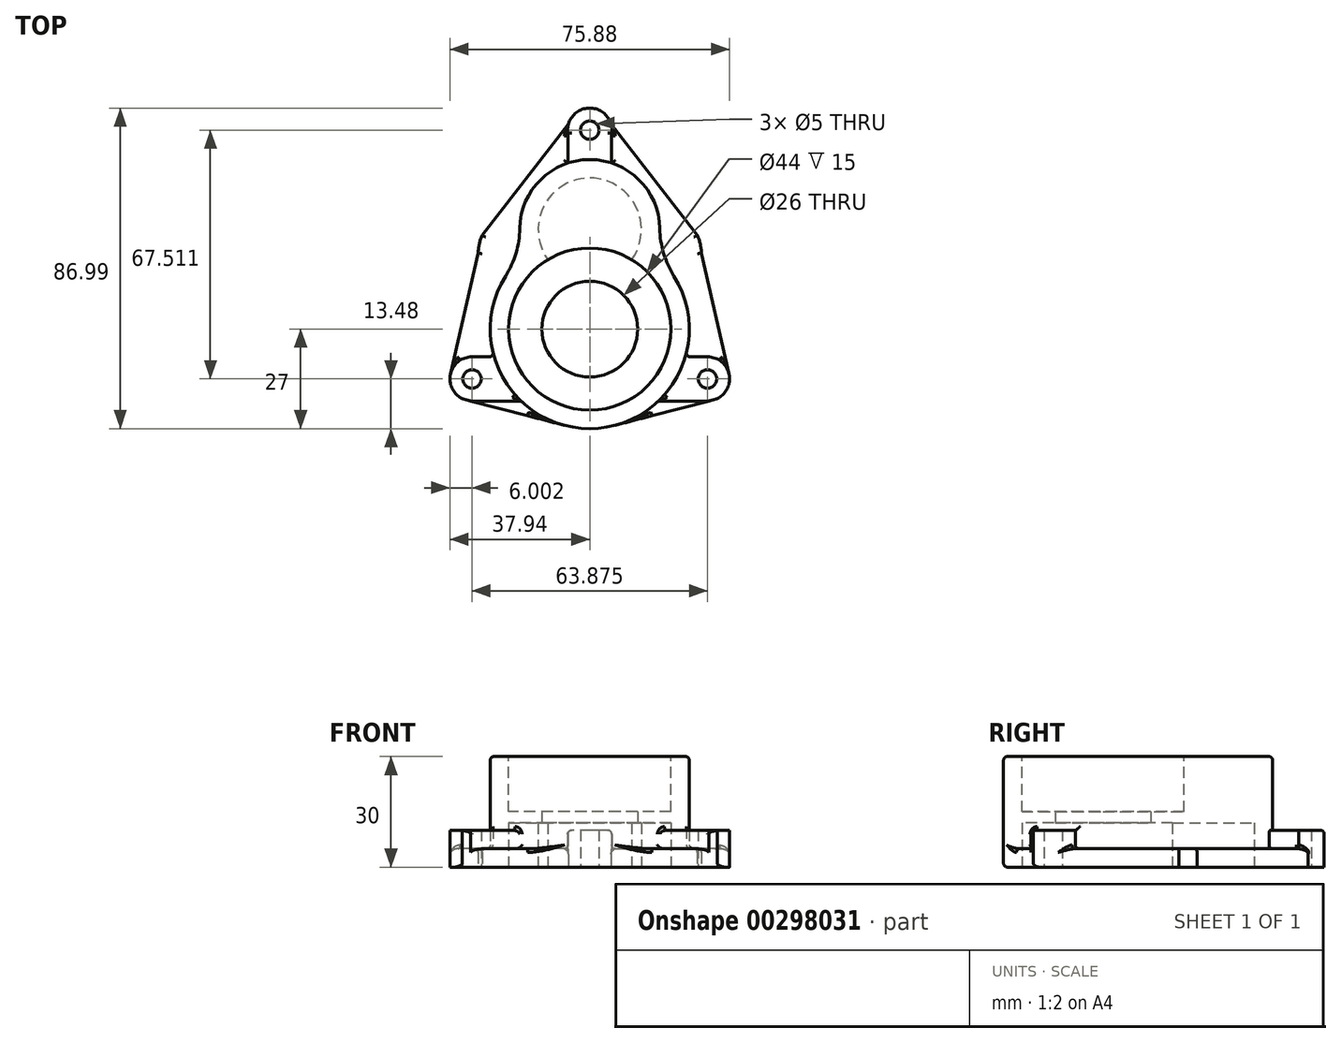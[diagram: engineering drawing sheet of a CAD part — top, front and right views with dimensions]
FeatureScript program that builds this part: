
annotation { "Feature Type Name" : "Feature", "Feature Type Description" : "" }
export const myFeature = defineFeature(function(context is Context, id is Id, definition is map)
    precondition{}
    {
        {
            var Q0;
            Q0=qCreatedBy(makeId("Top.planeOp"),FACE);
            var sketch = newSketch(context, id + "F0", { "sketchPlane" : qUnion([Q0])});
            skCircle(sketch, "E0", {"center": v(0, 0) * mm, "radius": 27 * mm});
            skArc(sketch, "E1", {"start": v(17.79, 20.31) * mm, "mid": v(0, 46) * mm, "end": v(-17.79, 20.31) * mm});
            skCircle(sketch, "E2", {"center": v(-31.94, -13.52) * mm, "radius": 6 * mm});
            skCircle(sketch, "E3", {"center": v(31.94, -13.52) * mm, "radius": 6 * mm});
            skCircle(sketch, "E4", {"center": v(-31.94, -13.52) * mm, "radius": 2.5 * mm});
            skCircle(sketch, "E5", {"center": v(31.94, -13.52) * mm, "radius": 2.5 * mm});
            skLineSegment(sketch, "E6", {"start": v(31.94, -7.52) * mm, "end": v(25.93, -7.52) * mm});
            skLineSegment(sketch, "E7", {"start": v(31.94, -19.52) * mm, "end": v(18.65, -19.52) * mm});
            skLineSegment(sketch, "E8", {"start": v(-31.94, -19.52) * mm, "end": v(-18.65, -19.52) * mm});
            skLineSegment(sketch, "E9", {"start": v(-31.94, -7.52) * mm, "end": v(-25.93, -7.52) * mm});
            skCircle(sketch, "E10", {"center": v(0, 54) * mm, "radius": 6 * mm});
            skPoint(sketch, "E10.centerSnap0", {"position": v(0, 46) * mm});
            skCircle(sketch, "E11", {"center": v(0, 54) * mm, "radius": 2.5 * mm});
            skLineSegment(sketch, "E12", {"start": v(-5.94, 53.11) * mm, "end": v(-5.94, 45.05) * mm});
            skLineSegment(sketch, "E13", {"start": v(5.94, 53.11) * mm, "end": v(5.94, 45.05) * mm});
            skCircle(sketch, "E14", {"center": v(0, 0) * mm, "radius": 13 * mm});
            skCircle(sketch, "E15", {"center": v(0, 0) * mm, "radius": 22 * mm});
            skPoint(sketch, "E16.orphan", {"position": v(-32, -44.07) * mm});
            skPoint(sketch, "E17.orphan", {"position": v(32, -45.38) * mm});
            skCircle(sketch, "E18", {"center": v(0, 27) * mm, "radius": 14 * mm});
            skArc(sketch, "E19", {"start": v(-29.16, 25.5) * mm, "mid": v(-29.97, 23.1) * mm, "end": v(-30.28, 20.6) * mm});
            skLineSegment(sketch, "E20", {"start": v(5.77, 55.62) * mm, "end": v(29.16, 25.5) * mm});
            skLineSegment(sketch, "E21", {"start": v(30.28, 20.6) * mm, "end": v(37.79, -12.18) * mm});
            skLineSegment(sketch, "E22", {"start": v(-5.77, 55.62) * mm, "end": v(-29.16, 25.5) * mm});
            skLineSegment(sketch, "E23", {"start": v(-30.28, 20.6) * mm, "end": v(-37.79, -12.18) * mm});
            skLineSegment(sketch, "E24", {"start": v(-34.56, -18.91) * mm, "end": v(-6.8, -26.13) * mm});
            skLineSegment(sketch, "E25", {"start": v(6.8, -26.13) * mm, "end": v(34.56, -18.91) * mm});
            skPoint(sketch, "E26.orphan", {"position": v(0, -27.9) * mm});
            skArc(sketch, "E27.trimOffspring", {"start": v(30.28, 20.6) * mm, "mid": v(29.97, 23.1) * mm, "end": v(29.16, 25.5) * mm});
            skSolve(sketch);
        }
        {
            var Q0;
            {var subQ0=sQuery(id+"F0.wireOp",EDGE,"E1");var subQ3=sQuery(id+"F0.wireOp",EDGE,"E0");var subQ4=makeQuery(id+"F0.imprint","INTERSECT",VERTEX,{"disambiguationData":[OD(0.0)],"derivedFrom":[subQ3,subQ0]});Q0=makeQuery(id+"F0.imprint","IMPRINT",FACE,{"disambiguationData":[TD([[makeQuery(id+"F0.imprint","IMPRINT",EDGE,{"disambiguationData":[TD([[subQ4,-1.0]])],"derivedFrom":subQ3}),-1.0]])]});}
            var Q1;
            {var subQ0=sQuery(id+"F0.wireOp",EDGE,"E1");var subQ1=sQuery(id+"F0.wireOp",EDGE,"E0");var subQ2=makeQuery(id+"F0.imprint","INTERSECT",VERTEX,{"disambiguationData":[OD(0.0)],"derivedFrom":[subQ1,subQ0]});Q1=makeQuery(id+"F0.imprint","IMPRINT",FACE,{"disambiguationData":[TD([[makeQuery(id+"F0.imprint","IMPRINT",EDGE,{"disambiguationData":[TD([[subQ2,-1.0]])],"derivedFrom":subQ1}),1.0]])]});}
            var Q2;
            {var subQ0=sQuery(id+"F0.wireOp",EDGE,"E18");var subQ1=sQuery(id+"F0.wireOp",EDGE,"E0");var subQ2=makeQuery(id+"F0.imprint","INTERSECT",VERTEX,{"disambiguationData":[OD(0.0)],"derivedFrom":[subQ1,subQ0]});Q2=makeQuery(id+"F0.imprint","IMPRINT",FACE,{"disambiguationData":[TD([[makeQuery(id+"F0.imprint","IMPRINT",EDGE,{"disambiguationData":[TD([[subQ2,-1.0]])],"derivedFrom":subQ1}),-1.0]])]});}
            var Q3;
            {var subQ0=sQuery(id+"F0.wireOp",EDGE,"E18");var subQ1=sQuery(id+"F0.wireOp",EDGE,"E0");var subQ2=makeQuery(id+"F0.imprint","INTERSECT",VERTEX,{"disambiguationData":[OD(0.0)],"derivedFrom":[subQ1,subQ0]});Q3=makeQuery(id+"F0.imprint","IMPRINT",FACE,{"disambiguationData":[TD([[makeQuery(id+"F0.imprint","IMPRINT",EDGE,{"disambiguationData":[TD([[subQ2,-1.0]])],"derivedFrom":subQ1}),1.0]])]});}
            var Q4;
            {var subQ0=sQuery(id+"F0.wireOp",EDGE,"E18");var subQ1=sQuery(id+"F0.wireOp",EDGE,"E15");var subQ2=makeQuery(id+"F0.imprint","INTERSECT",VERTEX,{"disambiguationData":[OD(0.0)],"derivedFrom":[subQ1,subQ0]});Q4=makeQuery(id+"F0.imprint","IMPRINT",FACE,{"disambiguationData":[TD([[makeQuery(id+"F0.imprint","IMPRINT",EDGE,{"disambiguationData":[TD([[subQ2,1.0]])],"derivedFrom":subQ1}),1.0]])]});}
            var Q5;
            Q5=makeQuery(id+"F0.imprint","IMPRINT",FACE,{"disambiguationData":[TD([[makeQuery(id+"F0.imprint","IMPRINT",EDGE,{"derivedFrom":sQuery(id+"F0.wireOp",EDGE,"E14")}),1.0]])]});
            var Q6;
            {var subQ0=sQuery(id+"F0.wireOp",EDGE,"E14");Q6=makeQuery(id+"F0.imprint","IMPRINT",FACE,{"disambiguationData":[TD([[makeQuery(id+"F0.imprint","IMPRINT",EDGE,{"derivedFrom":subQ0}),-1.0]])]});}
            extrude(context, id + "F1", {"entities" : qUnion([Q0, Q1, Q2, Q3, Q4, Q5, Q6]), "depth" : 30 * mm});
        }
        {
            var Q0;
            {var subQ0=sQuery(id+"F0.wireOp",EDGE,"E1");var subQ1=sQuery(id+"F0.wireOp",EDGE,"E0");Q0=makeQuery(id+"F1.opExtrude","SWEPT_EDGE",EDGE,{"disambiguationData":[OSD([subQ1,subQ0]),TDD([makeQuery(id+"F0.imprint","INTERSECT",VERTEX,{"disambiguationData":[OD(1.0)],"derivedFrom":[subQ1,subQ0]})])]});}
            var Q1;
            {var subQ0=sQuery(id+"F0.wireOp",EDGE,"E1");var subQ1=sQuery(id+"F0.wireOp",EDGE,"E0");Q1=makeQuery(id+"F1.opExtrude","SWEPT_EDGE",EDGE,{"disambiguationData":[OSD([subQ1,subQ0]),TDD([makeQuery(id+"F0.imprint","INTERSECT",VERTEX,{"disambiguationData":[OD(0.0)],"derivedFrom":[subQ1,subQ0]})])]});}
            fillet(context, id + "F2", {"entities" : qUnion([Q0, Q1]), "radius" : 25 * mm, "tangentPropagation" : true, "allowEdgeOverflow" : false});
        }
        {
            var Q0;
            {var subQ0=sQuery(id+"F0.wireOp",EDGE,"E12");Q0=makeQuery(id+"F0.imprint","IMPRINT",FACE,{"disambiguationData":[TD([[makeQuery(id+"F0.imprint","IMPRINT",EDGE,{"derivedFrom":subQ0}),1.0]])]});}
            var Q1;
            Q1=makeQuery(id+"F0.imprint","IMPRINT",FACE,{"disambiguationData":[TD([[makeQuery(id+"F0.imprint","IMPRINT",EDGE,{"derivedFrom":sQuery(id+"F0.wireOp",EDGE,"E11")}),-1.0]])]});
            var Q2;
            Q2=makeQuery(id+"F0.imprint","IMPRINT",FACE,{"disambiguationData":[TD([[makeQuery(id+"F0.imprint","IMPRINT",EDGE,{"derivedFrom":sQuery(id+"F0.wireOp",EDGE,"E5")}),-1.0]])]});
            var Q3;
            {var subQ0=sQuery(id+"F0.wireOp",EDGE,"E6");Q3=makeQuery(id+"F0.imprint","IMPRINT",FACE,{"disambiguationData":[TD([[makeQuery(id+"F0.imprint","IMPRINT",EDGE,{"derivedFrom":subQ0}),1.0]])]});}
            var Q4;
            Q4=makeQuery(id+"F0.imprint","IMPRINT",FACE,{"disambiguationData":[TD([[makeQuery(id+"F0.imprint","IMPRINT",EDGE,{"derivedFrom":sQuery(id+"F0.wireOp",EDGE,"E4")}),-1.0]])]});
            var Q5;
            {var subQ0=sQuery(id+"F0.wireOp",EDGE,"E8");Q5=makeQuery(id+"F0.imprint","IMPRINT",FACE,{"disambiguationData":[TD([[makeQuery(id+"F0.imprint","IMPRINT",EDGE,{"derivedFrom":subQ0}),1.0]])]});}
            extrude(context, id + "F3", {"entities" : qUnion([Q0, Q1, Q2, Q3, Q4, Q5]), "operationType" : NewBodyOperationType.ADD, "depth" : 10 * mm});
        }
        {
            var Q0;
            {var subQ4=sQuery(id+"F0.wireOp",EDGE,"E9");Q0=makeQuery(id+"F0.imprint","IMPRINT",FACE,{"disambiguationData":[TD([[makeQuery(id+"F0.imprint","IMPRINT",EDGE,{"derivedFrom":subQ4}),1.0]])]});}
            var Q1;
            {var subQ0=sQuery(id+"F0.wireOp",EDGE,"E6");Q1=makeQuery(id+"F0.imprint","IMPRINT",FACE,{"disambiguationData":[TD([[makeQuery(id+"F0.imprint","IMPRINT",EDGE,{"derivedFrom":subQ0}),-1.0]])]});}
            var Q2;
            {var subQ0=sQuery(id+"F0.wireOp",EDGE,"E7");Q2=makeQuery(id+"F0.imprint","IMPRINT",FACE,{"disambiguationData":[TD([[makeQuery(id+"F0.imprint","IMPRINT",EDGE,{"derivedFrom":subQ0}),1.0]])]});}
            var Q3;
            {var subQ0=sQuery(id+"F0.wireOp",EDGE,"E8");Q3=makeQuery(id+"F0.imprint","IMPRINT",FACE,{"disambiguationData":[TD([[makeQuery(id+"F0.imprint","IMPRINT",EDGE,{"derivedFrom":subQ0}),-1.0]])]});}
            extrude(context, id + "F4", {"entities" : qUnion([Q0, Q1, Q2, Q3]), "operationType" : NewBodyOperationType.ADD, "depth" : 5 * mm});
        }
        {
            var Q0;
            {var subQ0=sQuery(id+"F0.wireOp",EDGE,"E18");var subQ1=sQuery(id+"F0.wireOp",EDGE,"E0");var subQ2=makeQuery(id+"F0.imprint","INTERSECT",VERTEX,{"disambiguationData":[OD(0.0)],"derivedFrom":[subQ1,subQ0]});Q0=makeQuery(id+"F0.imprint","IMPRINT",FACE,{"disambiguationData":[TD([[makeQuery(id+"F0.imprint","IMPRINT",EDGE,{"disambiguationData":[TD([[subQ2,-1.0]])],"derivedFrom":subQ1}),-1.0]])]});}
            var Q1;
            {var subQ0=sQuery(id+"F0.wireOp",EDGE,"E18");var subQ1=sQuery(id+"F0.wireOp",EDGE,"E0");var subQ2=makeQuery(id+"F0.imprint","INTERSECT",VERTEX,{"disambiguationData":[OD(0.0)],"derivedFrom":[subQ1,subQ0]});Q1=makeQuery(id+"F0.imprint","IMPRINT",FACE,{"disambiguationData":[TD([[makeQuery(id+"F0.imprint","IMPRINT",EDGE,{"disambiguationData":[TD([[subQ2,-1.0]])],"derivedFrom":subQ1}),1.0]])]});}
            var Q2;
            {var subQ0=sQuery(id+"F0.wireOp",EDGE,"E18");var subQ1=sQuery(id+"F0.wireOp",EDGE,"E15");var subQ2=makeQuery(id+"F0.imprint","INTERSECT",VERTEX,{"disambiguationData":[OD(0.0)],"derivedFrom":[subQ1,subQ0]});Q2=makeQuery(id+"F0.imprint","IMPRINT",FACE,{"disambiguationData":[TD([[makeQuery(id+"F0.imprint","IMPRINT",EDGE,{"disambiguationData":[TD([[subQ2,1.0]])],"derivedFrom":subQ1}),1.0]])]});}
            var Q3;
            {var subQ0=sQuery(id+"F0.wireOp",EDGE,"E14");Q3=makeQuery(id+"F0.imprint","IMPRINT",FACE,{"disambiguationData":[TD([[makeQuery(id+"F0.imprint","IMPRINT",EDGE,{"derivedFrom":subQ0}),-1.0]])]});}
            var Q4;
            Q4=makeQuery(id+"F0.imprint","IMPRINT",FACE,{"disambiguationData":[TD([[makeQuery(id+"F0.imprint","IMPRINT",EDGE,{"derivedFrom":sQuery(id+"F0.wireOp",EDGE,"E14")}),1.0]])]});
            extrude(context, id + "F5", {"entities" : qUnion([Q0, Q1, Q2, Q3, Q4]), "operationType" : NewBodyOperationType.REMOVE, "depth" : 12 * mm});
        }
        {
            var Q0;
            Q0=makeQuery(id+"F1.opExtrude","CAP_FACE",FACE,{"disambiguationData":[OSD([sQuery(id+"F0.wireOp",EDGE,"E0"),sQuery(id+"F0.wireOp",EDGE,"E1")])],"isStart":false});
            var sketch = newSketch(context, id + "F6", { "sketchPlane" : qUnion([Q0])});
            skCircle(sketch, "E28.0", {"center": v(0, 0) * mm, "radius": 22 * mm});
            skSolve(sketch);
        }
        {
            var Q0;
            Q0=makeQuery(id+"F6.imprint","IMPRINT",FACE,{"disambiguationData":[TD([[makeQuery(id+"F6.imprint","IMPRINT",EDGE,{"derivedFrom":sQuery(id+"F6.wireOp",EDGE,"E28.0")}),1.0]])]});
            var Q1;
            Q1=sQuery(id+"F6.wireOp",EDGE,"E28.0");
            extrude(context, id + "F7", {"entities" : qUnion([Q0]), "operationType" : NewBodyOperationType.REMOVE, "surfaceEntities" : qUnion([Q1]), "oppositeDirection" : true, "depth" : 15 * mm});
        }
        {
            var Q0;
            Q0=makeQuery(id+"F0.imprint","IMPRINT",FACE,{"disambiguationData":[TD([[makeQuery(id+"F0.imprint","IMPRINT",EDGE,{"derivedFrom":sQuery(id+"F0.wireOp",EDGE,"E14")}),1.0]])]});
            extrude(context, id + "F8", {"entities" : qUnion([Q0]), "operationType" : NewBodyOperationType.REMOVE, "endBound" : BoundingType.THROUGH_ALL, "depth" : 25 * mm});
        }
        {
            var Q0;
            Q0=makeQuery(id+"F1.opExtrude","SWEPT_FACE",FACE,{"disambiguationData":[OSD([sQuery(id+"F0.wireOp",EDGE,"E0")])]});
            var Q1;
            Q1=makeQuery(id+"F4.opExtrude","CAP_FACE",FACE,{"disambiguationData":[OSD([sQuery(id+"F0.wireOp",EDGE,"E0"),sQuery(id+"F0.wireOp",EDGE,"E1"),sQuery(id+"F0.wireOp",EDGE,"E3"),sQuery(id+"F0.wireOp",EDGE,"E6"),sQuery(id+"F0.wireOp",EDGE,"E10"),sQuery(id+"F0.wireOp",EDGE,"E13"),sQuery(id+"F0.wireOp",EDGE,"E20"),sQuery(id+"F0.wireOp",EDGE,"E21"),sQuery(id+"F0.wireOp",EDGE,"E27.trimOffspring")])],"isStart":false});
            var Q2;
            Q2=makeQuery(id+"F3.opExtrude","CAP_EDGE",EDGE,{"disambiguationData":[OSD([sQuery(id+"F0.wireOp",EDGE,"E13")])],"isStart":false});
            var Q3;
            Q3=makeQuery(id+"F4.opExtrude","CAP_FACE",FACE,{"disambiguationData":[OSD([sQuery(id+"F0.wireOp",EDGE,"E0"),sQuery(id+"F0.wireOp",EDGE,"E1"),sQuery(id+"F0.wireOp",EDGE,"E2"),sQuery(id+"F0.wireOp",EDGE,"E9"),sQuery(id+"F0.wireOp",EDGE,"E10"),sQuery(id+"F0.wireOp",EDGE,"E12"),sQuery(id+"F0.wireOp",EDGE,"E19"),sQuery(id+"F0.wireOp",EDGE,"E22"),sQuery(id+"F0.wireOp",EDGE,"E23")])],"isStart":false});
            var Q4;
            Q4=makeQuery(id+"F3.opExtrude","CAP_EDGE",EDGE,{"disambiguationData":[OSD([sQuery(id+"F0.wireOp",EDGE,"E7")])],"isStart":false});
            var Q5;
            Q5=makeQuery(id+"F4.opExtrude","CAP_EDGE",EDGE,{"disambiguationData":[OSD([sQuery(id+"F0.wireOp",EDGE,"E7")])],"isStart":false});
            var Q6;
            Q6=makeQuery(id+"F3.opExtrude","CAP_EDGE",EDGE,{"disambiguationData":[OSD([sQuery(id+"F0.wireOp",EDGE,"E8")])],"isStart":false});
            var Q7;
            Q7=makeQuery(id+"F4.opExtrude","CAP_EDGE",EDGE,{"disambiguationData":[OSD([sQuery(id+"F0.wireOp",EDGE,"E8")])],"isStart":false});
            fillet(context, id + "F9", {"entities" : qUnion([Q0, Q1, Q2, Q3, Q4, Q5, Q6, Q7]), "radius" : 1 * mm, "tangentPropagation" : true, "allowEdgeOverflow" : false});
        }
        {
            var Q0;
            Q0=makeQuery(id+"F4.opExtrude","CAP_EDGE",EDGE,{"disambiguationData":[OSD([sQuery(id+"F0.wireOp",EDGE,"E24")])],"isStart":false});
            var Q1;
            {var subQ0=sQuery(id+"F0.wireOp",EDGE,"E24");var subQ1=sQuery(id+"F0.wireOp",EDGE,"E0");Q1=makeQuery(id+"F9.opFillet","BLEND_EDGE",EDGE,{"blendedFrom":[makeQuery(id+"F4.opExtrude","CAP_EDGE",EDGE,{"disambiguationData":[OSD([subQ1]),TDD([makeQuery(id+"F0.imprint","IMPRINT",EDGE,{"disambiguationData":[TD([[makeQuery(id+"F0.imprint","INTERSECT",VERTEX,{"derivedFrom":[subQ1,sQuery(id+"F0.wireOp",EDGE,"E8")]}),-1.0]])],"derivedFrom":subQ1})])],"isStart":false}),makeQuery(id+"F4.boolean.opBoolean","MERGE",FACE,{"derivedFrom":[makeQuery(id+"F3.opExtrude","SWEPT_FACE",FACE,{"disambiguationData":[OSD([subQ0])]}),makeQuery(id+"F4.opExtrude","SWEPT_FACE",FACE,{"disambiguationData":[OSD([subQ0])]})]})],"blendedInto":[makeQuery(id+"F4.boolean.opBoolean","MERGE",FACE,{"derivedFrom":[makeQuery(id+"F3.opExtrude","SWEPT_FACE",FACE,{"disambiguationData":[OSD([subQ0])]}),makeQuery(id+"F4.opExtrude","SWEPT_FACE",FACE,{"disambiguationData":[OSD([subQ0])]})]})]});}
            var Q2;
            {var subQ0=sQuery(id+"F0.wireOp",EDGE,"E25");var subQ1=sQuery(id+"F0.wireOp",EDGE,"E0");Q2=makeQuery(id+"F9.opFillet","BLEND_EDGE",EDGE,{"blendedFrom":[makeQuery(id+"F4.opExtrude","CAP_EDGE",EDGE,{"disambiguationData":[OSD([subQ1]),TDD([makeQuery(id+"F0.imprint","IMPRINT",EDGE,{"disambiguationData":[TD([[makeQuery(id+"F0.imprint","INTERSECT",VERTEX,{"derivedFrom":[subQ1,sQuery(id+"F0.wireOp",EDGE,"E7")]}),1.0]])],"derivedFrom":subQ1})])],"isStart":false}),makeQuery(id+"F4.boolean.opBoolean","MERGE",FACE,{"derivedFrom":[makeQuery(id+"F3.opExtrude","SWEPT_FACE",FACE,{"disambiguationData":[OSD([subQ0])]}),makeQuery(id+"F4.opExtrude","SWEPT_FACE",FACE,{"disambiguationData":[OSD([subQ0])]})]})],"blendedInto":[makeQuery(id+"F4.boolean.opBoolean","MERGE",FACE,{"derivedFrom":[makeQuery(id+"F3.opExtrude","SWEPT_FACE",FACE,{"disambiguationData":[OSD([subQ0])]}),makeQuery(id+"F4.opExtrude","SWEPT_FACE",FACE,{"disambiguationData":[OSD([subQ0])]})]})]});}
            var Q3;
            Q3=makeQuery(id+"F4.opExtrude","CAP_EDGE",EDGE,{"disambiguationData":[OSD([sQuery(id+"F0.wireOp",EDGE,"E25")])],"isStart":false});
            var Q4;
            {var subQ0=sQuery(id+"F0.wireOp",EDGE,"E25");Q4=makeQuery(id+"F9.opFillet","BLEND_EDGE",EDGE,{"blendedFrom":[makeQuery(id+"F4.opExtrude","CAP_EDGE",EDGE,{"disambiguationData":[OSD([sQuery(id+"F0.wireOp",EDGE,"E7")])],"isStart":false}),makeQuery(id+"F4.boolean.opBoolean","MERGE",FACE,{"derivedFrom":[makeQuery(id+"F3.opExtrude","SWEPT_FACE",FACE,{"disambiguationData":[OSD([subQ0])]}),makeQuery(id+"F4.opExtrude","SWEPT_FACE",FACE,{"disambiguationData":[OSD([subQ0])]})]})],"blendedInto":[makeQuery(id+"F4.boolean.opBoolean","MERGE",FACE,{"derivedFrom":[makeQuery(id+"F3.opExtrude","SWEPT_FACE",FACE,{"disambiguationData":[OSD([subQ0])]}),makeQuery(id+"F4.opExtrude","SWEPT_FACE",FACE,{"disambiguationData":[OSD([subQ0])]})]})]});}
            fillet(context, id + "F10", {"entities" : qUnion([Q0, Q1, Q2, Q3, Q4]), "radius" : 1 * mm, "tangentPropagation" : true, "allowEdgeOverflow" : false});
        }
        {
            var Q0;
            Q0=makeQuery(id+"F3.opExtrude","CAP_EDGE",EDGE,{"disambiguationData":[OSD([sQuery(id+"F0.wireOp",EDGE,"E12")])],"isStart":false});
            var Q1;
            Q1=makeQuery(id+"F3.opExtrude","CAP_EDGE",EDGE,{"disambiguationData":[OSD([sQuery(id+"F0.wireOp",EDGE,"E10")])],"isStart":false});
            fillet(context, id + "F11", {"entities" : qUnion([Q0, Q1]), "radius" : 1 * mm, "tangentPropagation" : true, "allowEdgeOverflow" : false});
        }
    });
